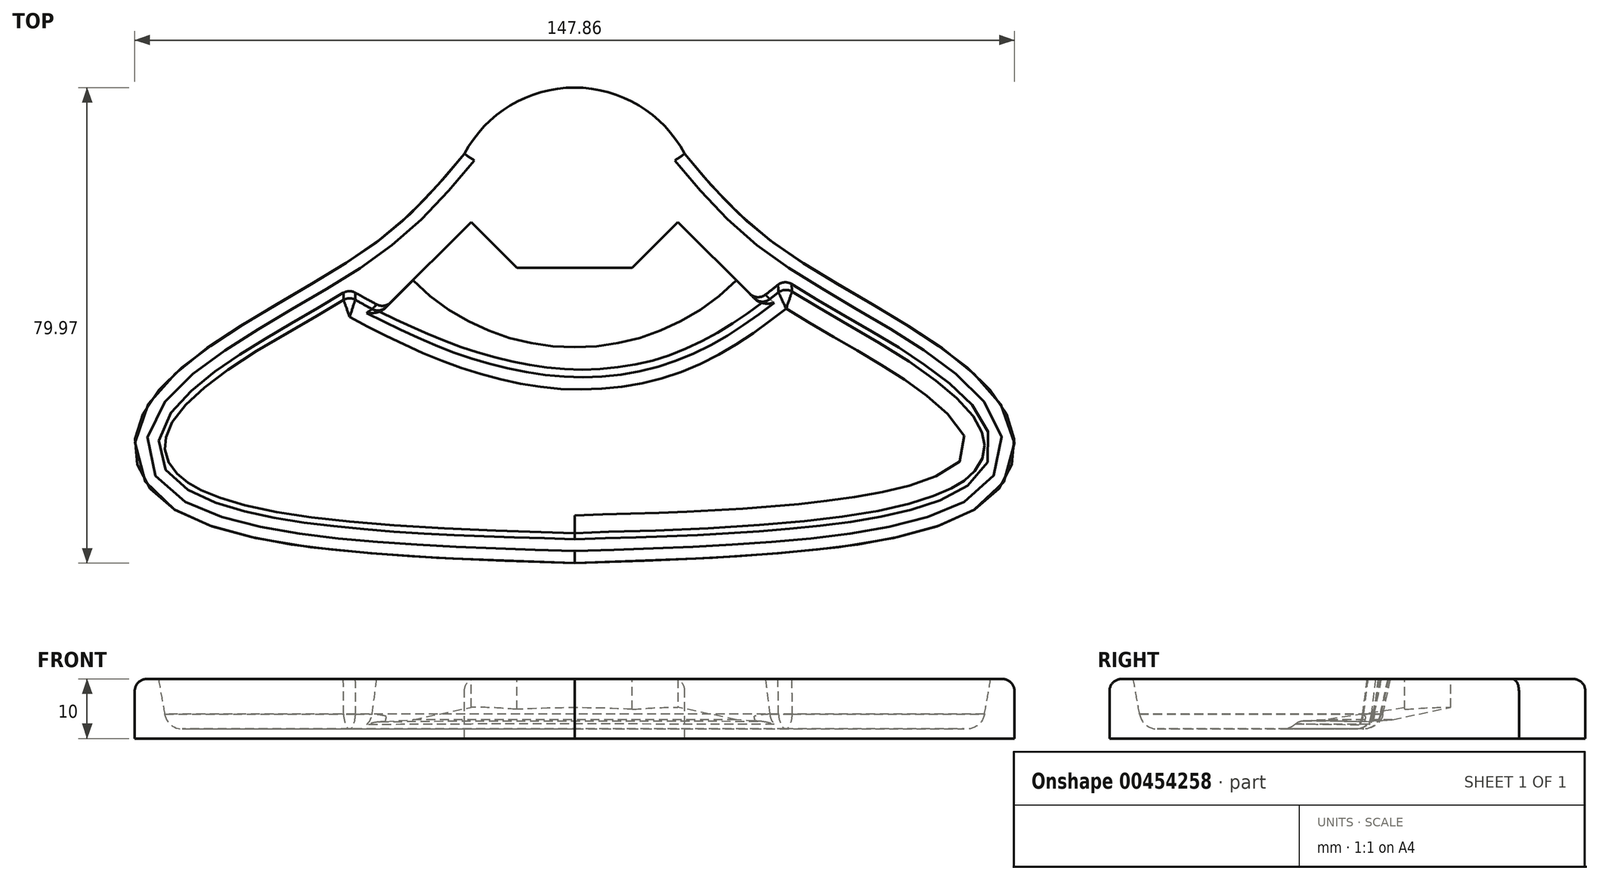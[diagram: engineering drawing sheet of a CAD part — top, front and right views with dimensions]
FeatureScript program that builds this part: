
annotation { "Feature Type Name" : "Feature", "Feature Type Description" : "" }
export const myFeature = defineFeature(function(context is Context, id is Id, definition is map)
    precondition{}
    {
        {
            var Q0;
            Q0=qCreatedBy(makeId("Top.planeOp"),FACE);
            var sketch = newSketch(context, id + "F0", { "sketchPlane" : qUnion([Q0])});
            skArc(sketch, "E0", {"start": v(18.51, 9.8) * mm, "mid": v(10.8, 17.94) * mm, "end": v(0, 20.95) * mm});
            skLineSegment(sketch, "E1", {"start": v(0, 34.4) * mm, "end": v(0, -34.61) * mm, "construction": true});
            skFitSpline(sketch, "E2", {"points": [v(18.51, 9.8) * mm, v(32.77, -4.67) * mm, v(59.9, -21.6) * mm, v(73.56, -36.56) * mm, v(67.92, -49.58) * mm, v(0, -59.02) * mm], "startDerivative": vector(72.31, -87.12) * mm, "endDerivative": vector(-269.24, -9.23) * mm});
            skFitSpline(sketch, "E3.MirrorCS", {"points": [v(-18.51, 9.8) * mm, v(-32.77, -4.67) * mm, v(-59.9, -21.6) * mm, v(-73.56, -36.56) * mm, v(-67.92, -49.58) * mm, v(0, -59.02) * mm], "startDerivative": vector(-72.31, -87.12) * mm, "endDerivative": vector(269.24, -9.23) * mm});
            skArc(sketch, "E4.MirrorCS", {"start": v(-18.51, 9.8) * mm, "mid": v(-10.8, 17.94) * mm, "end": v(0, 20.95) * mm});
            skSolve(sketch);
        }
        {
            var Q0;
            Q0=makeQuery(id+"F0.imprint","IMPRINT",FACE,{"disambiguationData":[TD([[makeQuery(id+"F0.imprint","IMPRINT",EDGE,{"derivedFrom":sQuery(id+"F0.wireOp",EDGE,"E0")}),1.0]])]});
            extrude(context, id + "F1", {"entities" : qUnion([Q0]), "oppositeDirection" : true, "depth" : 10 * mm});
        }
        {
            var Q0;
            Q0=makeQuery(id+"F1.opExtrude","CAP_FACE",FACE,{"disambiguationData":[OSD([sQuery(id+"F0.wireOp",EDGE,"E0"),sQuery(id+"F0.wireOp",EDGE,"E2"),sQuery(id+"F0.wireOp",EDGE,"E3.MirrorCS"),sQuery(id+"F0.wireOp",EDGE,"E4.MirrorCS")])],"isStart":true});
            var sketch = newSketch(context, id + "F2", { "sketchPlane" : qUnion([Q0])});
            skFitSpline(sketch, "E5", {"points": [v(-38.08, -8.34) * mm, v(-12.63, -19.78) * mm, v(13.18, -20.03) * mm, v(35.1, -6.36) * mm], "startDerivative": vector(72.53, -39.35) * mm, "endDerivative": vector(63.27, 50.81) * mm});
            skSolve(sketch);
        }
        {
            var Q0;
            {var subQ0=sQuery(id+"F2.wireOp",EDGE,"E5");Q0=makeQuery(id+"F2.imprint","IMPRINT",FACE,{"disambiguationData":[TD([[makeQuery(id+"F2.imprint","IMPRINT",EDGE,{"derivedFrom":subQ0}),-1.0]])]});}
            var sketch = newSketch(context, id + "F3", { "sketchPlane" : qUnion([Q0])});
            skFitSpline(sketch, "E6.0", {"points": [v(37.61, -9.48) * mm, v(36.3, -10.54) * mm, v(33.63, -12.68) * mm, v(29.52, -15.81) * mm, v(25.21, -18.76) * mm, v(21.42, -20.93) * mm, v(18.23, -22.43) * mm, v(15.75, -23.42) * mm, v(13.18, -24.24) * mm, v(10.57, -24.87) * mm, v(7.91, -25.33) * mm, v(4.34, -25.72) * mm, v(-0.17, -25.82) * mm, v(-5.58, -25.37) * mm, v(-10.04, -24.56) * mm, v(-13.55, -23.7) * mm, v(-17, -22.67) * mm, v(-21.2, -21.16) * mm, v(-26.06, -19.06) * mm, v(-32.38, -15.99) * mm, v(-36.97, -13.5) * mm, v(-39.99, -11.86) * mm]});
            skFitSpline(sketch, "E6.1", {"points": [v(-0.14, -55.03) * mm, v(5.48, -54.83) * mm, v(16.74, -54.47) * mm, v(30.18, -53.75) * mm, v(40.07, -52.86) * mm, v(46.93, -52) * mm, v(53.12, -50.9) * mm, v(57.59, -49.78) * mm, v(60.67, -48.75) * mm, v(62.72, -47.92) * mm, v(64.2, -47.18) * mm, v(65.22, -46.58) * mm, v(66.13, -45.97) * mm, v(67.12, -45.2) * mm, v(68.05, -44.23) * mm, v(68.78, -43.27) * mm, v(69.48, -41.99) * mm, v(69.85, -40.71) * mm, v(69.95, -39.42) * mm, v(69.88, -38.43) * mm, v(69.68, -37.44) * mm, v(69.2, -36.07) * mm, v(68.2, -34.22) * mm, v(66.29, -31.86) * mm, v(63.73, -29.42) * mm, v(60.62, -26.95) * mm, v(55.9, -23.66) * mm, v(50.5, -20.4) * mm, v(44.87, -17.12) * mm, v(40.63, -14.64) * mm, v(36.5, -12.1) * mm, v(33.2, -9.93) * mm, v(31.02, -8.36) * mm, v(29.81, -7.45) * mm, v(28.06, -6.07) * mm, v(25.63, -3.97) * mm, v(22.74, -1.13) * mm, v(20.12, 1.7) * mm, v(17.71, 4.5) * mm, v(16.19, 6.34) * mm, v(15.44, 7.24) * mm]});
            skFitSpline(sketch, "E6.2", {"points": [v(-15.44, 7.24) * mm, v(-16.19, 6.34) * mm, v(-17.71, 4.5) * mm, v(-20.12, 1.7) * mm, v(-22.74, -1.13) * mm, v(-25.63, -3.97) * mm, v(-28.06, -6.07) * mm, v(-29.81, -7.45) * mm, v(-31.02, -8.36) * mm, v(-33.2, -9.93) * mm, v(-36.5, -12.1) * mm, v(-40.63, -14.64) * mm, v(-44.87, -17.12) * mm, v(-50.5, -20.4) * mm, v(-55.9, -23.66) * mm, v(-60.62, -26.95) * mm, v(-63.73, -29.42) * mm, v(-66.29, -31.86) * mm, v(-68.2, -34.22) * mm, v(-69.2, -36.07) * mm, v(-69.68, -37.44) * mm, v(-69.88, -38.43) * mm, v(-69.95, -39.42) * mm, v(-69.85, -40.71) * mm, v(-69.48, -41.99) * mm, v(-68.78, -43.27) * mm, v(-68.05, -44.23) * mm, v(-67.12, -45.2) * mm, v(-66.13, -45.97) * mm, v(-65.22, -46.58) * mm, v(-64.2, -47.18) * mm, v(-62.72, -47.92) * mm, v(-60.67, -48.75) * mm, v(-57.59, -49.78) * mm, v(-53.12, -50.9) * mm, v(-46.93, -52) * mm, v(-40.07, -52.86) * mm, v(-30.18, -53.75) * mm, v(-16.74, -54.47) * mm, v(-5.48, -54.83) * mm, v(0.14, -55.03) * mm]});
            skSolve(sketch);
        }
        {
            var Q0;
            Q0=makeQuery(id+"F3.imprint","IMPRINT",FACE,{"disambiguationData":[TD([[makeQuery(id+"F3.imprint","IMPRINT",EDGE,{"derivedFrom":sQuery(id+"F3.wireOp",EDGE,"E6.0")}),1.0]])]});
            extrude(context, id + "F4", {"entities" : qUnion([Q0]), "operationType" : NewBodyOperationType.REMOVE, "oppositeDirection" : true, "depth" : 8.4 * mm, "hasDraft" : true, "draftAngle" : 10 * degree, "draftPullDirection" : true});
        }
        {
            var Q0;
            Q0=makeQuery(id+"F4.boolean.opBoolean","COPY",EDGE,{"derivedFrom":makeQuery(id+"F4.opExtrude","CAP_EDGE",EDGE,{"disambiguationData":[OSD([sQuery(id+"F3.wireOp",EDGE,"E6.2")])],"isStart":false})});
            var Q1;
            Q1=makeQuery(id+"F4.boolean.opBoolean","COPY",FACE,{"derivedFrom":makeQuery(id+"F4.opExtrude","CAP_FACE",FACE,{"disambiguationData":[OSD([sQuery(id+"F3.wireOp",EDGE,"E6.0"),sQuery(id+"F3.wireOp",EDGE,"E6.1"),sQuery(id+"F3.wireOp",EDGE,"E6.2")])],"isStart":false})});
            fillet(context, id + "F5", {"entities" : qUnion([Q0, Q1]), "radius" : 3 * mm, "tangentPropagation" : true, "allowEdgeOverflow" : false});
        }
        {
            var Q0;
            Q0=makeQuery(id+"F1.opExtrude","CAP_EDGE",EDGE,{"disambiguationData":[OSD([sQuery(id+"F0.wireOp",EDGE,"E3.MirrorCS")])],"isStart":true});
            var Q1;
            Q1=makeQuery(id+"F1.opExtrude","CAP_EDGE",EDGE,{"disambiguationData":[OSD([sQuery(id+"F0.wireOp",EDGE,"E2")])],"isStart":true});
            var Q2;
            Q2=makeQuery(id+"F1.opExtrude","CAP_EDGE",EDGE,{"disambiguationData":[OSD([sQuery(id+"F0.wireOp",EDGE,"E0"),sQuery(id+"F0.wireOp",EDGE,"E4.MirrorCS")])],"isStart":true});
            fillet(context, id + "F6", {"entities" : qUnion([Q0, Q1, Q2]), "radius" : 2 * mm, "tangentPropagation" : true, "allowEdgeOverflow" : false});
        }
        {
            var Q0;
            Q0=qCreatedBy(makeId("Right.planeOp"),FACE);
            var sketch = newSketch(context, id + "F7", { "sketchPlane" : qUnion([Q0])});
            skLineSegment(sketch, "E7", {"start": v(15.7, 10.1) * mm, "end": v(15.7, -5.39) * mm, "construction": true});
            skLineSegment(sketch, "E8", {"start": v(15.7, -1.05) * mm, "end": v(15.7, 2.35) * mm});
            skLineSegment(sketch, "E9", {"start": v(15.7, 2.35) * mm, "end": v(-35.1, 3.46) * mm});
            skLineSegment(sketch, "E10", {"start": v(-35.1, 3.46) * mm, "end": v(-32.44, -7.3) * mm});
            skLineSegment(sketch, "E11", {"start": v(-32.44, -7.3) * mm, "end": v(-22.73, -6.85) * mm});
            skLineSegment(sketch, "E12", {"start": v(-22.73, -6.85) * mm, "end": v(15.7, -1.05) * mm});
            skSolve(sketch);
        }
        {
            var Q0;
            Q0 = qSketchRegion(id + "F7", true);
            var Q1;
            Q1=sQuery(id+"F7.wireOp",EDGE,"E7");
            revolve(context, id + "F8", {"operationType" : NewBodyOperationType.REMOVE, "entities" : qUnion([Q0]), "axis" : qUnion([Q1]), "revolveType" : RevolveType.SYMMETRIC, "oppositeDirection" : true, "angle" : 90 * degree});
        }
        {
            var Q0;
            Q0=makeQuery(id+"F8.boolean.opBoolean","INTERSECT",EDGE,{"derivedFrom":[makeQuery(id+"F4.boolean.opBoolean","COPY",FACE,{"derivedFrom":makeQuery(id+"F4.opExtrude","SWEPT_FACE",FACE,{"disambiguationData":[OSD([sQuery(id+"F3.wireOp",EDGE,"E6.0")])]})}),makeQuery(id+"F8.opRevolve","CAP_FACE",FACE,{"disambiguationData":[OSD([sQuery(id+"F7.wireOp",EDGE,"E8"),sQuery(id+"F7.wireOp",EDGE,"E9"),sQuery(id+"F7.wireOp",EDGE,"E10"),sQuery(id+"F7.wireOp",EDGE,"E11"),sQuery(id+"F7.wireOp",EDGE,"E12")])],"isStart":true})]});
            var Q1;
            Q1=makeQuery(id+"F4.boolean.opBoolean","COPY",EDGE,{"derivedFrom":makeQuery(id+"F4.opExtrude","SWEPT_EDGE",EDGE,{"disambiguationData":[OSD([sQuery(id+"F3.wireOp",EDGE,"E6.0"),sQuery(id+"F3.wireOp",EDGE,"E6.2")])]})});
            var Q2;
            Q2=makeQuery(id+"F4.boolean.opBoolean","COPY",EDGE,{"derivedFrom":makeQuery(id+"F4.opExtrude","SWEPT_EDGE",EDGE,{"disambiguationData":[OSD([sQuery(id+"F3.wireOp",EDGE,"E6.0"),sQuery(id+"F3.wireOp",EDGE,"E6.1")])]})});
            var Q3;
            Q3=makeQuery(id+"F8.boolean.opBoolean","INTERSECT",EDGE,{"derivedFrom":[makeQuery(id+"F4.boolean.opBoolean","COPY",FACE,{"derivedFrom":makeQuery(id+"F4.opExtrude","SWEPT_FACE",FACE,{"disambiguationData":[OSD([sQuery(id+"F3.wireOp",EDGE,"E6.0")])]})}),makeQuery(id+"F8.opRevolve","CAP_FACE",FACE,{"disambiguationData":[OSD([sQuery(id+"F7.wireOp",EDGE,"E8"),sQuery(id+"F7.wireOp",EDGE,"E9"),sQuery(id+"F7.wireOp",EDGE,"E10"),sQuery(id+"F7.wireOp",EDGE,"E11"),sQuery(id+"F7.wireOp",EDGE,"E12")])],"isStart":false})]});
            fillet(context, id + "F9", {"entities" : qUnion([Q0, Q1, Q2, Q3]), "radius" : 2 * mm, "tangentPropagation" : true, "allowEdgeOverflow" : false});
        }
        {
            var Q0;
            Q0=makeQuery(id+"F8.boolean.opBoolean","INTERSECT",EDGE,{"derivedFrom":[makeQuery(id+"F5.opFillet","BLEND_FACE",FACE,{"disambiguationData":[OSD([sQuery(id+"F3.wireOp",EDGE,"E6.0")])]}),makeQuery(id+"F8.opRevolve","SWEPT_FACE",FACE,{"disambiguationData":[OSD([sQuery(id+"F7.wireOp",EDGE,"E11")])]})]});
            fillet(context, id + "F10", {"entities" : qUnion([Q0]), "radius" : 2 * mm, "tangentPropagation" : true, "allowEdgeOverflow" : false});
        }
        {
            var Q0;
            Q0=qCreatedBy(makeId("Top.planeOp"),FACE);
            var sketch = newSketch(context, id + "F11", { "sketchPlane" : qUnion([Q0])});
            skLineSegment(sketch, "E13", {"start": v(9.7, -9.39) * mm, "end": v(19.71, 0.72) * mm});
            skLineSegment(sketch, "E14", {"start": v(19.71, 0.72) * mm, "end": v(13.87, 7.45) * mm});
            skLineSegment(sketch, "E15", {"start": v(13.87, 7.45) * mm, "end": v(0, 17.21) * mm});
            skLineSegment(sketch, "E16.MirrorCS", {"start": v(-9.7, -9.39) * mm, "end": v(-19.71, 0.72) * mm});
            skLineSegment(sketch, "E17.MirrorCS", {"start": v(-13.87, 7.45) * mm, "end": v(0, 17.21) * mm});
            skLineSegment(sketch, "E18.MirrorCS", {"start": v(-19.71, 0.72) * mm, "end": v(-13.87, 7.45) * mm});
            skLineSegment(sketch, "E19", {"start": v(9.7, -9.39) * mm, "end": v(-9.7, -9.39) * mm});
            skSolve(sketch);
        }
        {
            var Q0;
            Q0 = qSketchRegion(id + "F11", true);
            extrude(context, id + "F12", {"entities" : qUnion([Q0]), "operationType" : NewBodyOperationType.ADD, "oppositeDirection" : true, "depth" : 8.6 * mm});
        }
    });
